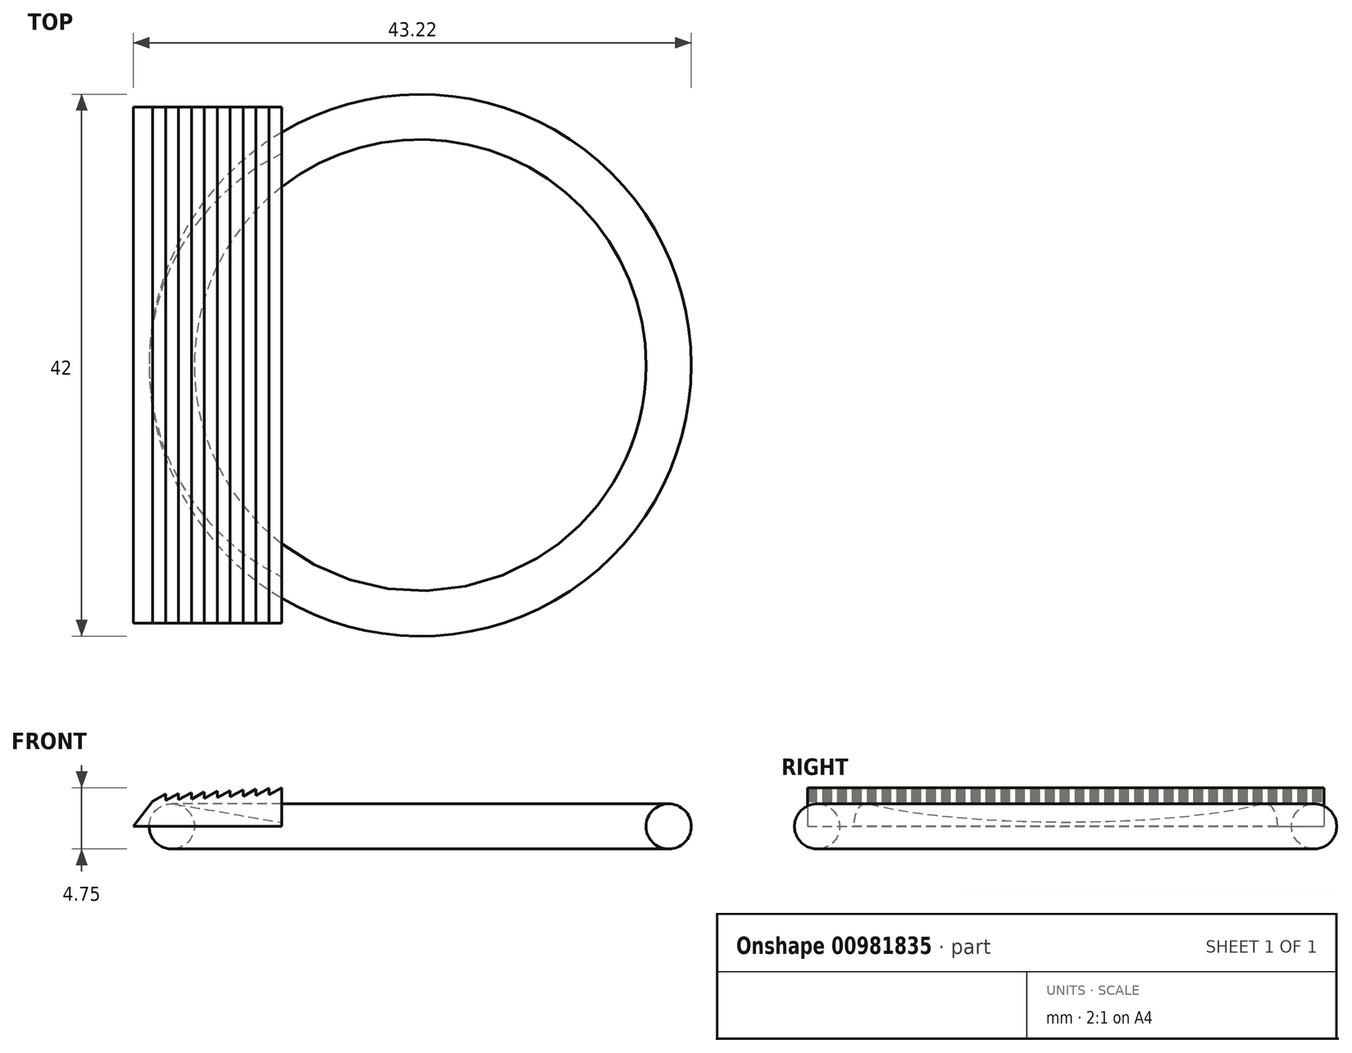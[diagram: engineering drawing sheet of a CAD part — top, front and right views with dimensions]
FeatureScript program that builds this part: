
annotation { "Feature Type Name" : "Feature", "Feature Type Description" : "" }
export const myFeature = defineFeature(function(context is Context, id is Id, definition is map)
    precondition{}
    {
        {
            var Q0;
            Q0=qCreatedBy(makeId("Front.planeOp"),FACE);
            var sketch = newSketch(context, id + "F0", { "sketchPlane" : qUnion([Q0])});
            skLineSegment(sketch, "E0", {"start": v(-22.22, 0) * mm, "end": v(-22.22, 0) * mm});
            skLineSegment(sketch, "E1", {"start": v(-15.72, 2.73) * mm, "end": v(-15.72, 2.23) * mm});
            skLineSegment(sketch, "E2", {"start": v(-15.72, 2.23) * mm, "end": v(-14.72, 2.78) * mm});
            skLineSegment(sketch, "E3", {"start": v(-14.72, 2.78) * mm, "end": v(-14.72, 2.28) * mm});
            skLineSegment(sketch, "E4", {"start": v(-10.72, 2.5) * mm, "end": v(-10.72, 0) * mm});
            skLineSegment(sketch, "E5", {"start": v(-29.04, 2) * mm, "end": v(-10.72, 3) * mm, "construction": true});
            skLineSegment(sketch, "E6", {"start": v(-29.04, 1.5) * mm, "end": v(-10.72, 2.5) * mm, "construction": true});
            skLineSegment(sketch, "E7", {"start": v(-14.72, 2.28) * mm, "end": v(-13.72, 2.84) * mm});
            skLineSegment(sketch, "E8", {"start": v(-13.72, 2.84) * mm, "end": v(-13.72, 2.34) * mm});
            skLineSegment(sketch, "E9", {"start": v(-13.72, 2.34) * mm, "end": v(-12.72, 2.9) * mm});
            skLineSegment(sketch, "E10", {"start": v(-12.72, 2.9) * mm, "end": v(-12.72, 2.4) * mm});
            skLineSegment(sketch, "E11", {"start": v(-12.72, 2.4) * mm, "end": v(-11.72, 2.95) * mm});
            skLineSegment(sketch, "E12", {"start": v(-11.72, 2.95) * mm, "end": v(-11.72, 2.45) * mm});
            skLineSegment(sketch, "E13", {"start": v(-11.72, 2.45) * mm, "end": v(-10.72, 3) * mm});
            skLineSegment(sketch, "E14", {"start": v(-10.72, 2.5) * mm, "end": v(-10.72, 3) * mm});
            skLineSegment(sketch, "E15", {"start": v(-15.72, 2.73) * mm, "end": v(-16.72, 2.17) * mm});
            skLineSegment(sketch, "E16", {"start": v(-16.72, 2.17) * mm, "end": v(-16.72, 2.67) * mm});
            skLineSegment(sketch, "E17", {"start": v(-16.72, 2.67) * mm, "end": v(-17.72, 2.12) * mm});
            skLineSegment(sketch, "E18", {"start": v(-17.72, 2.12) * mm, "end": v(-17.72, 2.62) * mm});
            skLineSegment(sketch, "E19", {"start": v(-17.72, 2.62) * mm, "end": v(-18.72, 2.06) * mm});
            skLineSegment(sketch, "E20", {"start": v(-18.72, 2.06) * mm, "end": v(-18.72, 2.56) * mm});
            skLineSegment(sketch, "E21", {"start": v(-18.72, 2.56) * mm, "end": v(-19.72, 2) * mm});
            skLineSegment(sketch, "E22", {"start": v(-19.72, 2) * mm, "end": v(-19.72, 2.5) * mm});
            skLineSegment(sketch, "E23", {"start": v(-19.72, 2.5) * mm, "end": v(-20.72, 1.95) * mm});
            skLineSegment(sketch, "E24", {"start": v(-20.72, 1.95) * mm, "end": v(-22.22, 0) * mm});
            skLineSegment(sketch, "E25", {"start": v(-22.22, 0) * mm, "end": v(-10.72, 0) * mm});
            skSolve(sketch);
        }
        {
            var Q0;
            Q0=makeQuery(id+"F0.imprint","IMPRINT",FACE,{"disambiguationData":[TD([[makeQuery(id+"F0.imprint","IMPRINT",EDGE,{"derivedFrom":sQuery(id+"F0.wireOp",EDGE,"E1")}),-1.0]])]});
            extrude(context, id + "F1", {"entities" : qUnion([Q0]), "endBound" : BoundingType.SYMMETRIC, "depth" : 40 * mm, "offsetDistance" : 25 * mm});
        }
        {
            var Q0;
            Q0=qCreatedBy(makeId("Top.planeOp"),FACE);
            var sketch = newSketch(context, id + "F2", { "sketchPlane" : qUnion([Q0])});
            skCircle(sketch, "E26", {"center": v(0, 0) * mm, "radius": 18.25 * mm});
            skArc(sketch, "E27", {"start": v(0, 18.25) * mm, "mid": v(-18.25, 0) * mm, "end": v(0, -18.25) * mm});
            skSolve(sketch);
        }
        {
            var Q0;
            Q0=qCreatedBy(makeId("Front.planeOp"),FACE);
            var sketch = newSketch(context, id + "F3", { "sketchPlane" : qUnion([Q0])});
            skCircle(sketch, "E28", {"center": v(-19.25, 0) * mm, "radius": 1.75 * mm});
            skLineSegment(sketch, "E29", {"start": v(0, 0) * mm, "end": v(-10.25, 0) * mm, "construction": true});
            skLineSegment(sketch, "E30", {"start": v(-10.25, 0) * mm, "end": v(-10.25, 0.22) * mm});
            skLineSegment(sketch, "E31", {"start": v(-10.25, 0.22) * mm, "end": v(-18.95, 1.72) * mm});
            skLineSegment(sketch, "E32", {"start": v(-19.25, 0) * mm, "end": v(-10.25, 0) * mm, "construction": true});
            skLineSegment(sketch, "E33.MirrorCS", {"start": v(-10.25, -0.22) * mm, "end": v(-18.95, -1.72) * mm});
            skLineSegment(sketch, "E34.MirrorCS", {"start": v(-10.25, 0) * mm, "end": v(-10.25, -0.22) * mm});
            skSolve(sketch);
        }
        {
            var Q0;
            Q0=makeQuery(id+"F3.imprint","IMPRINT",FACE,{"disambiguationData":[TD([[makeQuery(id+"F3.imprint","IMPRINT",EDGE,{"derivedFrom":sQuery(id+"F3.wireOp",EDGE,"E28")}),1.0]])]});
            var Q1;
            Q1=sQuery(id+"F2.wireOp",EDGE,"E26");
            sweep(context, id + "F4", {"profiles" : qUnion([Q0]), "path" : qUnion([Q1])});
        }
        {
            var Q0;
            Q0=qCreatedBy(makeId("Top.planeOp"),FACE);
            var sketch = newSketch(context, id + "F5", { "sketchPlane" : qUnion([Q0])});
            skArc(sketch, "E35", {"start": v(0, 18.25) * mm, "mid": v(-18.25, 0) * mm, "end": v(0, -18.25) * mm});
            skSolve(sketch);
        }
        {
            var Q0;
            Q0=qSketchRegion(id+"F3",true);
            var Q1;
            Q1=qConstructionFilter(qBodyType(qCreatedBy(id+"F5",EDGE),BodyType.WIRE),ConstructionObject.NO);
            sweep(context, id + "F6", {"profiles" : qUnion([Q0]), "path" : qUnion([Q1]), "keepProfileOrientation" : true});
        }
        {
            var Q0;
            Q0=makeQuery(id+"F6.opSweep","SWEPT_BODY",BODY,{"disambiguationData":[OSD([sQuery(id+"F3.wireOp",EDGE,"E28"),sQuery(id+"F3.wireOp",EDGE,"E30"),sQuery(id+"F3.wireOp",EDGE,"E31"),sQuery(id+"F3.wireOp",EDGE,"E33.MirrorCS"),sQuery(id+"F3.wireOp",EDGE,"E34.MirrorCS"),sQuery(id+"F5.wireOp",EDGE,"E35")])]});
            var Q1;
            Q1=makeQuery(id+"F1.opExtrude","SWEPT_BODY",BODY,{"disambiguationData":[OSD([sQuery(id+"F0.wireOp",EDGE,"E1"),sQuery(id+"F0.wireOp",EDGE,"E2"),sQuery(id+"F0.wireOp",EDGE,"E3"),sQuery(id+"F0.wireOp",EDGE,"E4"),sQuery(id+"F0.wireOp",EDGE,"E7"),sQuery(id+"F0.wireOp",EDGE,"E8"),sQuery(id+"F0.wireOp",EDGE,"E9"),sQuery(id+"F0.wireOp",EDGE,"E10"),sQuery(id+"F0.wireOp",EDGE,"E11"),sQuery(id+"F0.wireOp",EDGE,"E12"),sQuery(id+"F0.wireOp",EDGE,"E13"),sQuery(id+"F0.wireOp",EDGE,"E14"),sQuery(id+"F0.wireOp",EDGE,"E15"),sQuery(id+"F0.wireOp",EDGE,"E16"),sQuery(id+"F0.wireOp",EDGE,"E17"),sQuery(id+"F0.wireOp",EDGE,"E18"),sQuery(id+"F0.wireOp",EDGE,"E19"),sQuery(id+"F0.wireOp",EDGE,"E20"),sQuery(id+"F0.wireOp",EDGE,"E21"),sQuery(id+"F0.wireOp",EDGE,"E22"),sQuery(id+"F0.wireOp",EDGE,"E23"),sQuery(id+"F0.wireOp",EDGE,"E24"),sQuery(id+"F0.wireOp",EDGE,"E25")])]});
            booleanBodies(context, id + "F7", {"operationType" : BooleanOperationType.SUBTRACTION, "tools" : qUnion([Q0]), "targets" : qUnion([Q1])});
        }
    });
